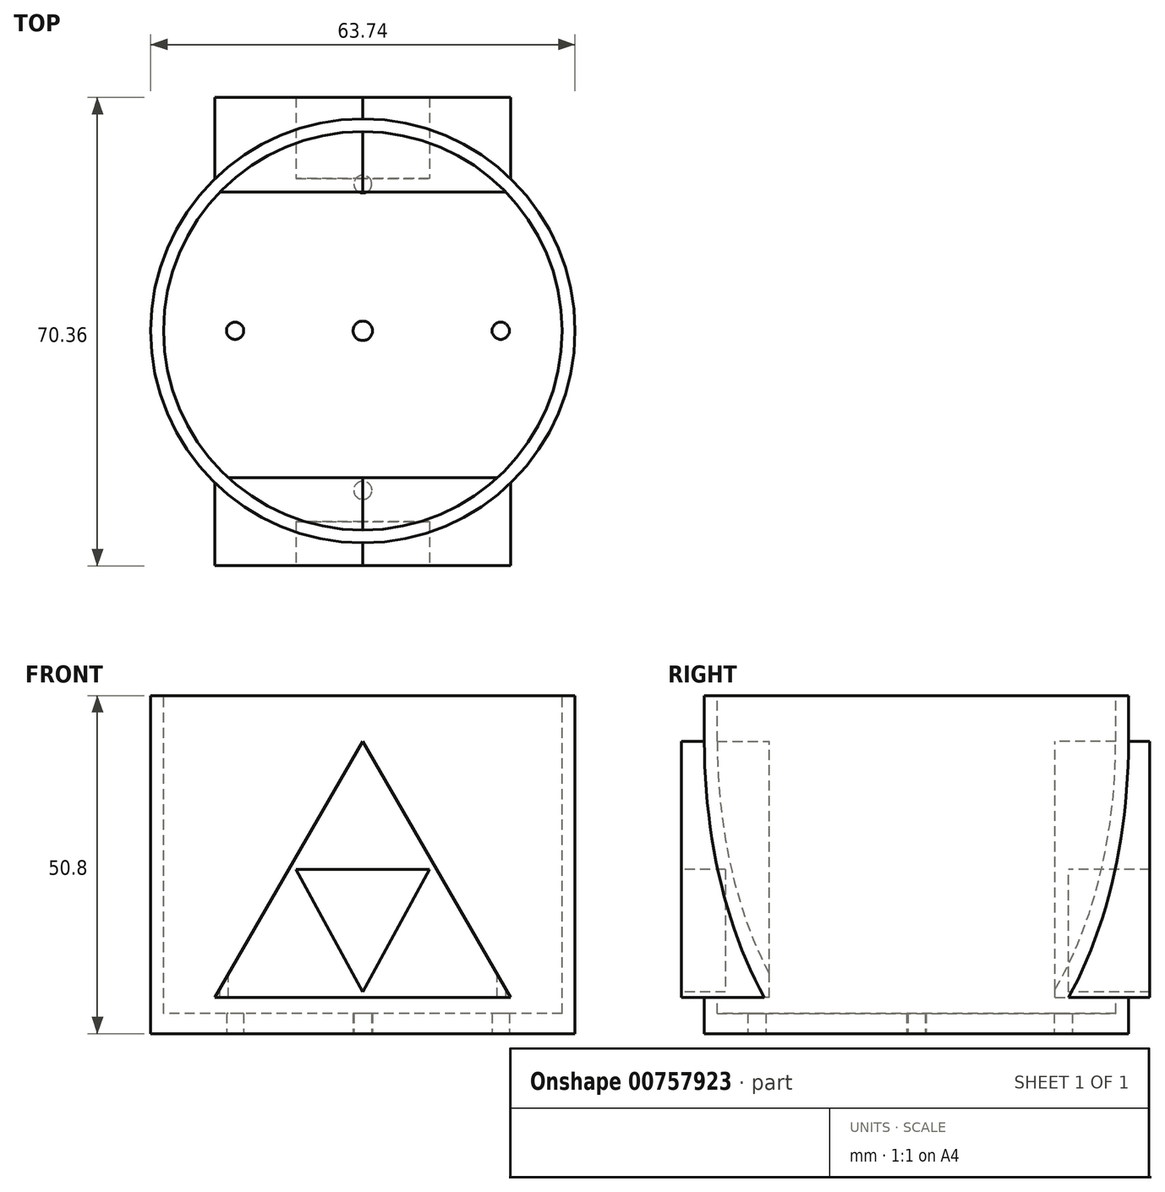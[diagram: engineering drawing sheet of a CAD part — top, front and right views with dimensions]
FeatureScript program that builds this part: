
annotation { "Feature Type Name" : "Feature", "Feature Type Description" : "" }
export const myFeature = defineFeature(function(context is Context, id is Id, definition is map)
    precondition{}
    {
        {
            var Q0;
            Q0=qCreatedBy(makeId("Top.planeOp"),FACE);
            var sketch = newSketch(context, id + "F0", { "sketchPlane" : qUnion([Q0])});
            skCircle(sketch, "E0", {"center": v(0, 0) * mm, "radius": 31.87 * mm});
            skSolve(sketch);
        }
        {
            var Q0;
            Q0=makeQuery(id+"F0.imprint","IMPRINT",FACE,{"disambiguationData":[TD([[makeQuery(id+"F0.imprint","IMPRINT",EDGE,{"derivedFrom":sQuery(id+"F0.wireOp",EDGE,"E0")}),1.0]])]});
            extrude(context, id + "F1", {"entities" : qUnion([Q0]), "depth" : 50.8 * mm, "offsetDistance" : 25.4 * mm});
        }
        {
            var Q0;
            Q0=makeQuery(id+"F1.opExtrude","CAP_FACE",FACE,{"disambiguationData":[OSD([sQuery(id+"F0.wireOp",EDGE,"E0")])],"isStart":false});
            var sketch = newSketch(context, id + "F2", { "sketchPlane" : qUnion([Q0])});
            skCircle(sketch, "E1", {"center": v(0, 0) * mm, "radius": 29.94 * mm});
            skSolve(sketch);
        }
        {
            var Q0;
            Q0=makeQuery(id+"F1.opExtrude","CAP_FACE",FACE,{"disambiguationData":[OSD([sQuery(id+"F0.wireOp",EDGE,"E0")])],"isStart":true});
            var sketch = newSketch(context, id + "F3", { "sketchPlane" : qUnion([Q0])});
            skCircle(sketch, "E2", {"center": v(0, 23.96) * mm, "radius": 1.37 * mm});
            skCircle(sketch, "E3", {"center": v(0, 0) * mm, "radius": 1.46 * mm});
            skCircle(sketch, "E4", {"center": v(0, -22.06) * mm, "radius": 1.34 * mm});
            skCircle(sketch, "E5", {"center": v(-19.2, 0) * mm, "radius": 1.3 * mm});
            skCircle(sketch, "E6", {"center": v(20.72, 0) * mm, "radius": 1.3 * mm});
            skSolve(sketch);
        }
        {
            var Q0;
            Q0 = qSketchRegion(id + "F2", true);
            extrude(context, id + "F4", {"entities" : qUnion([Q0]), "operationType" : NewBodyOperationType.REMOVE, "oppositeDirection" : true, "depth" : 47.75 * mm, "offsetDistance" : 25.4 * mm});
        }
        {
            var Q0;
            Q0 = qSketchRegion(id + "F3", true);
            extrude(context, id + "F5", {"entities" : qUnion([Q0]), "operationType" : NewBodyOperationType.REMOVE, "oppositeDirection" : true, "depth" : 25.4 * mm, "offsetDistance" : 25.4 * mm});
        }
        {
            var Q0;
            Q0 = qSketchRegion(id + "F3", true);
            extrude(context, id + "F6", {"entities" : qUnion([Q0]), "operationType" : NewBodyOperationType.REMOVE, "oppositeDirection" : true, "depth" : 25.4 * mm, "offsetDistance" : 25.4 * mm});
        }
        {
            var Q0;
            Q0=qCreatedBy(makeId("Front.planeOp"),FACE);
            var sketch = newSketch(context, id + "F7", { "sketchPlane" : qUnion([Q0])});
            skLineSegment(sketch, "E7", {"start": v(0, 43.92) * mm, "end": v(-22.23, 5.43) * mm});
            skLineSegment(sketch, "E8", {"start": v(-22.23, 5.43) * mm, "end": v(22.22, 5.43) * mm});
            skLineSegment(sketch, "E9", {"start": v(22.22, 5.43) * mm, "end": v(0, 43.92) * mm});
            skLineSegment(sketch, "E10", {"start": v(-11.11, 24.67) * mm, "end": v(11.11, 24.67) * mm});
            skLineSegment(sketch, "E11", {"start": v(11.11, 24.67) * mm, "end": v(0, 5.43) * mm});
            skLineSegment(sketch, "E12", {"start": v(0, 5.43) * mm, "end": v(-11.11, 24.67) * mm});
            skSolve(sketch);
        }
        {
            var Q0;
            Q0 = qSketchRegion(id + "F7", true);
            extrude(context, id + "F8", {"entities" : qUnion([Q0]), "operationType" : NewBodyOperationType.ADD, "depth" : 35.3 * mm, "offsetDistance" : 25.4 * mm, "hasSecondDirection" : true, "secondDirectionOppositeDirection" : false, "secondDirectionDepth" : 22.1 * mm});
        }
        {
            var Q0;
            Q0=makeQuery(id+"F8.opExtrude","CAP_FACE",FACE,{"disambiguationData":[OSD([sQuery(id+"F7.wireOp",EDGE,"E7"),sQuery(id+"F7.wireOp",EDGE,"E8"),sQuery(id+"F7.wireOp",EDGE,"E9")])],"isStart":false});
            var sketch = newSketch(context, id + "F9", { "sketchPlane" : qUnion([Q0])});
            skLineSegment(sketch, "E13", {"start": v(-10.05, 24.67) * mm, "end": v(10.03, 24.67) * mm});
            skPoint(sketch, "E13.startSnap0", {"position": v(-11.11, 24.67) * mm});
            skLineSegment(sketch, "E14", {"start": v(10.03, 24.67) * mm, "end": v(0, 6.27) * mm});
            skPoint(sketch, "E14.endSnap0", {"position": v(0, 5.43) * mm});
            skLineSegment(sketch, "E15", {"start": v(0, 6.27) * mm, "end": v(-10.05, 24.67) * mm});
            skSolve(sketch);
        }
        {
            var Q0;
            Q0 = qSketchRegion(id + "F9", true);
            extrude(context, id + "F10", {"entities" : qUnion([Q0]), "operationType" : NewBodyOperationType.REMOVE, "endBound" : BoundingType.THROUGH_ALL, "oppositeDirection" : true, "depth" : 25.4 * mm, "offsetDistance" : 25.4 * mm});
        }
        {
            var Q0;
            Q0 = qSketchRegion(id + "F7", true);
            extrude(context, id + "F11", {"entities" : qUnion([Q0]), "operationType" : NewBodyOperationType.ADD, "oppositeDirection" : true, "depth" : 35.05 * mm, "offsetDistance" : 25.4 * mm, "hasSecondDirection" : true, "secondDirectionOppositeDirection" : true, "secondDirectionDepth" : 20.83 * mm});
        }
        {
            var Q0;
            Q0 = qSketchRegion(id + "F9", true);
            extrude(context, id + "F12", {"entities" : qUnion([Q0]), "operationType" : NewBodyOperationType.REMOVE, "endBound" : BoundingType.THROUGH_ALL, "oppositeDirection" : true, "depth" : 25.4 * mm, "offsetDistance" : 25.4 * mm});
        }
        {
            var Q0;
            Q0=makeQuery(id+"F11.opExtrude","CAP_FACE",FACE,{"disambiguationData":[OSD([sQuery(id+"F7.wireOp",EDGE,"E7"),sQuery(id+"F7.wireOp",EDGE,"E8"),sQuery(id+"F7.wireOp",EDGE,"E9")])],"isStart":false});
            var sketch = newSketch(context, id + "F13", { "sketchPlane" : qUnion([Q0])});
            skLineSegment(sketch, "E16", {"start": v(-10.03, 24.67) * mm, "end": v(10.05, 24.67) * mm});
            skLineSegment(sketch, "E17", {"start": v(10.05, 24.67) * mm, "end": v(0, 6.27) * mm});
            skLineSegment(sketch, "E18", {"start": v(0, 6.27) * mm, "end": v(-10.03, 24.67) * mm});
            skSolve(sketch);
        }
        {
            var Q0;
            Q0 = qSketchRegion(id + "F13", true);
            var Q1;
            Q1=makeQuery(id+"F11.opExtrude","CAP_FACE",FACE,{"disambiguationData":[OSD([sQuery(id+"F7.wireOp",EDGE,"E7"),sQuery(id+"F7.wireOp",EDGE,"E8"),sQuery(id+"F7.wireOp",EDGE,"E9")])],"isStart":true});
            extrude(context, id + "F14", {"entities" : qUnion([Q0]), "operationType" : NewBodyOperationType.ADD, "endBound" : BoundingType.UP_TO_SURFACE, "oppositeDirection" : true, "depth" : 14.48 * mm, "endBoundEntityFace" : qUnion([Q1]), "offsetDistance" : 25.4 * mm, "hasSecondDirection" : true, "secondDirectionOppositeDirection" : true, "secondDirectionDepth" : 12.2 * mm});
        }
        {
            var Q0;
            Q0=makeQuery(id+"F8.opExtrude","CAP_FACE",FACE,{"disambiguationData":[OSD([sQuery(id+"F7.wireOp",EDGE,"E7"),sQuery(id+"F7.wireOp",EDGE,"E8"),sQuery(id+"F7.wireOp",EDGE,"E9")])],"isStart":false});
            var sketch = newSketch(context, id + "F15", { "sketchPlane" : qUnion([Q0])});
            skLineSegment(sketch, "E19", {"start": v(-10.05, 24.67) * mm, "end": v(10.03, 24.67) * mm});
            skLineSegment(sketch, "E20", {"start": v(10.03, 24.67) * mm, "end": v(0, 6.27) * mm});
            skLineSegment(sketch, "E21", {"start": v(0, 6.27) * mm, "end": v(-10.05, 24.67) * mm});
            skSolve(sketch);
        }
        {
            var Q0;
            Q0 = qSketchRegion(id + "F15", true);
            var Q1;
            Q1=makeQuery(id+"F8.opExtrude","CAP_FACE",FACE,{"disambiguationData":[OSD([sQuery(id+"F7.wireOp",EDGE,"E7"),sQuery(id+"F7.wireOp",EDGE,"E8"),sQuery(id+"F7.wireOp",EDGE,"E9")])],"isStart":true});
            extrude(context, id + "F16", {"entities" : qUnion([Q0]), "operationType" : NewBodyOperationType.ADD, "endBound" : BoundingType.UP_TO_SURFACE, "oppositeDirection" : true, "depth" : 25.4 * mm, "endBoundEntityFace" : qUnion([Q1]), "offsetDistance" : 25.4 * mm, "hasSecondDirection" : true, "secondDirectionOppositeDirection" : true, "secondDirectionDepth" : 6.6 * mm});
        }
    });
